# Revit family: IS_Linda-X_T4988_BIM_NL
name_source: partatom
category: Plumbing Fixtures
units: mm (PartAtom-declared; Revit-internal decimal feet)

## family parameters
Always vertical = No
Cut with Voids When Loaded = No
OmniClass Number = 23.45.05.14.14
OmniClass Title = Sinks/Lavatories
Part Type = Normal
Room Calculation Point = No
Round Connector Dimension = Use Diameter
Shared = No
Work Plane-Based = No

## types (3) — shared parameters
Accesoires = https://www.idealstandard.nll
Accessories = https://www.idealstandard.nll
Afmetingen = 600 x 500 x 135 mm
AfstandsEenheid = Millimeter
AreaUnits = millimetres
Artikelreferentie = LINDA-X BASIN 60CM 1 TAP HOLE
Auteur = Ideal Standard
BIMObjectName = IS_IdealStandard_Wall-hungwashbasins_LindaX_T4988
BIMobject category = Wash Basins
BIMobject category code = wash-basins
BIMobject main category = Sanitary
BIMobject main category code = sanitary
Beschrijvinggarantie = Herstellergarantie
BimObjectNaam = IS_IdealStandard_Wall-hungwashbasins_LindaX_T4988
Brand = Ideal Standard
Brand url = https://www.idealstandard.nl
Breedte = 599.94627
ConnectionType = Plumbing
CurrencyUnit = €
CurrentRevision = 1
Date of publishing = 30/09/2021
Diepte = 500 mm  [stored 1.64042 ft]
DurationUnit = Years
Edition number = 1
ElementType = Fixed
Help = https://www.idealstandard.co.uk
IFC Classification = Sanitary Terminal
IfcExportAs = IfcSanitaryTerminalType
IfcExportType = WASHHANDBASIN
Installation instructions = https://www.idealstandard.co.uk
InstallationInstructions = https://www.idealstandard.nll
IsBuiltIn = No
LinearUnits = millimetres
MaintenanceInformation = https://www.idealstandard.nll
Manufacturer = Ideal Standard
Manufacturer name = Ideal Standard
ManufacturerURL = https://www.idealstandard.nl
Materiaal = Fine Fire clay
Material = Fine Fire clay
Material main = Ceramics
Merk = Ideal Standard
ModelReference = LINDA-X BASIN 60CM 1 TAP HOLE
Montageinstuctie = https://www.idealstandard.nll
NBS Reference Code = 45-35-70/369
NBS Reference Description = Wall hung wash basins
Name = Wall-hungwashbasins_LindaX_T4988_IdealStandard
NominalDepth = 500 mm  [stored 1.64042 ft]
NominalHeight = 135 mm  [stored 0.442913 ft]
NominalWidth = 600 mm
OmniClass Code = 23-39 29 13 21 19
OmniClass Description = Surface Water Retention Basins
Ophangingwastafel = wandhängendes Waschbecken
OppervlakteEenheid = Millimeter
Product Guid = a1ed0ddf-1783-4e27-a7e6-b584462e2048
Product SKU = T4988
Product certification = https://www.idealstandard.nll
Product data url = https://bimobject.com
Product family = Sanitary
Product group = Washbasins
Product name = Linda
Product url = https://www.idealstandard.nll
ProductInformation = https://www.idealstandard.nll
Productinformatie = https://www.idealstandard.nll
QR code = http://bimobject.com
Revisie = 1
Shape = sculpture
Size = 600 x 500 x 135 mm
Space = Internal
SpareParts = https://www.idealstandard.nll
Technical description = https://www.idealstandard.nll
Telefoonnummer = 077 355 08 08
Typeconnectie = Installation
Typewastafel = wandhängendes Waschbecken
UNSPSC Code = 301815
URL = https://www.idealstandard.nll
Uniclass 1.4 Code = L7212
Uniclass 1.4 Description = Washbasins
Uniclass 2.0 Code = PR-31-79
Uniclass 2.0 Description = Sinks, Wash Basins And Troughs
Uniclass 2015 Code = Pr_40_20_96_96
Uniclass 2015 Name = Wall-hung wash basins
Uniclass2015Beschrijving = Wall-hung wash basins
Uniclass2015Code = Pr_40_20_96_96
Uniclass2015Referentie = Pr_40_20_96_96
Uniclass2015Title = Wall-hung washbasins
Uniclass2015Version = v1.22
Urlproducent = https://www.idealstandard.nll
ValutaEenheid = Euro
Versie = 1
Version = 1
VolumeUnits = Litres
Volumeunits = Liter
Vorm = gemeißelt
WarrantyDescription = manufacturer warranty
WarrantyDurationUnit = Years
WashHandBasinMounting = wall hung
WashHandBasinType = wall hung washbasin
Wisselstukken = https://www.idealstandard.nll
Youtube clip = https://www.youtube.com
zero-valued in all types: BrutoGewicht, Cost, DrainSize, Lengte, MaterialThickness, Nettogewicht, OutletConnectionSize, SpilloverLevel, Vervangingskosten

## per-type parameters (varying)
| type | Afwerking | Artikelnummer | Artikelomschrijving | BarCode | Barcode | Color | Description | Features | Finish | GTIN code | MainColor | Model | ModelNumber | NettWeight | Referentie |
| T4988V1 - LINDA-X BASIN 60CM, 1 TAP HOLE, WITHOUT OVERFLOW,AND GRINDED BOTTOM SIDE. SILK WHITE | Seidenweiß | T4988V1 | LINDA-X WASCHBECKEN 60CM, 1 HAHNLOCH, OHNE ÜBERLAUF UND UNTERSEITE geschliffen. SEIDE WEISS | 8014140492238 | 8014140492238 | Seidenweiß | LINDA-X BASIN 60CM, 1 TAP HOLE, WITHOUT OVERFLOW,AND GRINDED BOTTOM SIDE. SILK WHITE | BASIN 60CM, 1 TAP HOLE, WITHOUT OVERFLOW,AND GRINDED BOTTOM SIDE. SILK WHITE | Silk White | 8014140492238 | Silk White | T4988V1 | T4988V1 | 14,00 KG | T4988V1 |
| T4988MA - LINDA-X BASIN 60CM, 1 TAP HOLE, WITHOUT OVERFLOW,AND GRINDED BOTTOM SIDE. IDEAL PLUS GLOSS WHITE | Ideal Plus Glanzweiß | T4988MA | LINDA-X WASCHBECKEN 60CM, 1 HAHNLOCH, OHNE ÜBERLAUF UND UNTERSEITE geschliffen. IDEAL PLUS GLÄNZEND WEISS | 8014140492221 | 8014140492221 | Ideal Plus Glanzweiß | LINDA-X BASIN 60CM, 1 TAP HOLE, WITHOUT OVERFLOW,AND GRINDED BOTTOM SIDE. IDEAL PLUS GLOSS WHITE | BASIN 60CM, 1 TAP HOLE, WITHOUT OVERFLOW,AND GRINDED BOTTOM SIDE. IDEAL PLUS GLOSS WHITE | Ideal Plus Gloss White | 8014140492221 | Ideal Plus Gloss White | T4988MA | T4988MA | 0,00 KG | T4988MA |
| T498801 - LINDA-X BASIN 60CM, 1 TAP HOLE, WITHOUT OVERFLOW,AND GRINDED BOTTOM SIDE. WHITE | Weiß | T498801 | LINDA-X WASCHBECKEN 60CM, 1 HAHNLOCH, OHNE ÜBERLAUF UND UNTERSEITE geschliffen. WEISS | 8014140492214 | 8014140492214 | Weiß | LINDA-X BASIN 60CM, 1 TAP HOLE, WITHOUT OVERFLOW,AND GRINDED BOTTOM SIDE. WHITE | BASIN 60CM, 1 TAP HOLE, WITHOUT OVERFLOW,AND GRINDED BOTTOM SIDE. WHITE | White | 8014140492214 | White | T498801 | T498801 | 14,00 KG | T498801 |

note: [stored X ft] marks values corroborated as IEEE doubles in the binary element streams (Revit-internal decimal feet)

## geometry (parser evidence)
native form markers: Sweep x3
no freeform markers — native parametric forms only
